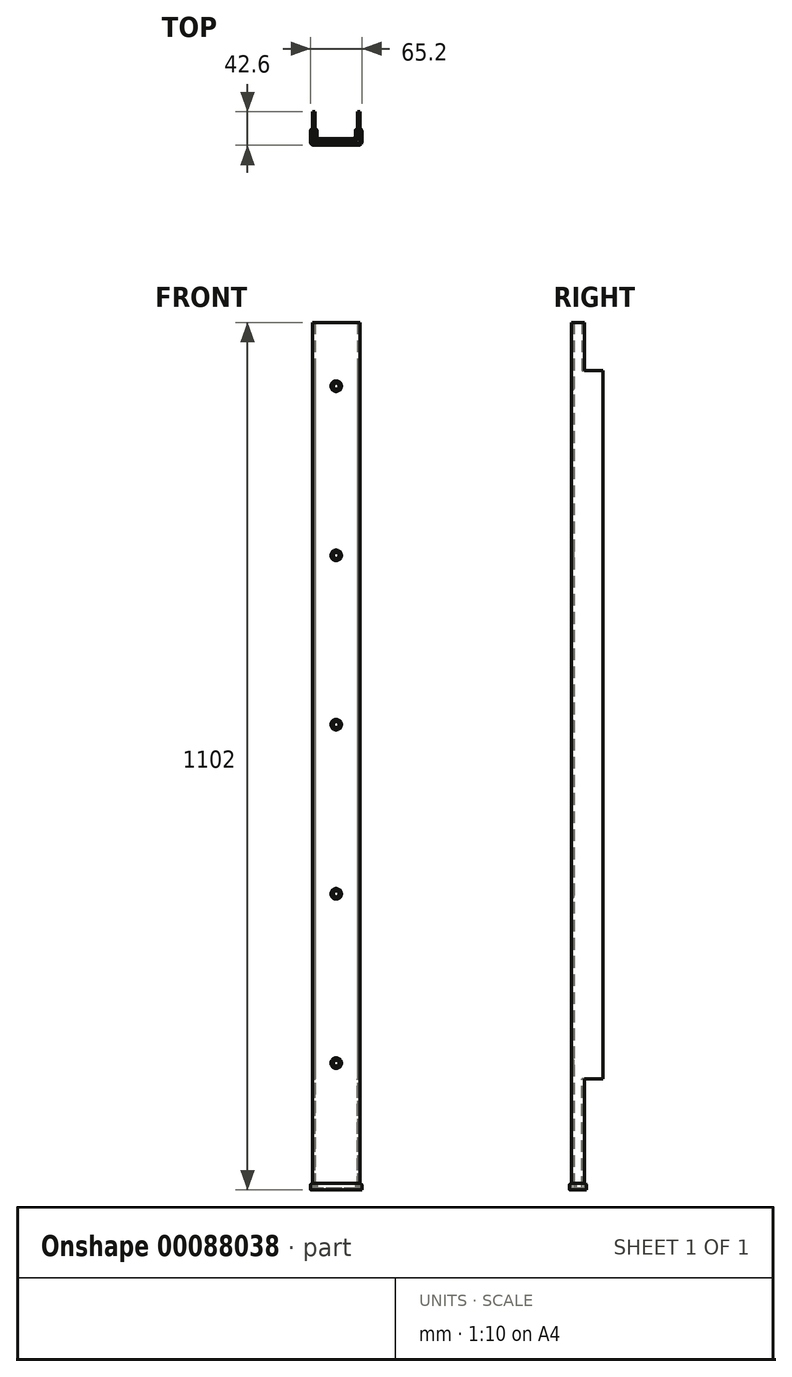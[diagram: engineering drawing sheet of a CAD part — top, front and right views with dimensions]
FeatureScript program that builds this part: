
annotation { "Feature Type Name" : "Feature", "Feature Type Description" : "" }
export const myFeature = defineFeature(function(context is Context, id is Id, definition is map)
    precondition{}
    {
        {
            var Q0;
            Q0=qCreatedBy(makeId("Top.planeOp"),FACE);
            var sketch = newSketch(context, id + "F0", { "sketchPlane" : qUnion([Q0])});
            skLineSegment(sketch, "E0", {"start": v(0, 0) * mm, "end": v(-60, 0) * mm});
            skLineSegment(sketch, "E1", {"start": v(-60, 0) * mm, "end": v(-60, 40) * mm});
            skLineSegment(sketch, "E2", {"start": v(0, 0) * mm, "end": v(0, 40) * mm});
            skLineSegment(sketch, "E3.0", {"start": v(-57, 3) * mm, "end": v(-57, 40) * mm});
            skLineSegment(sketch, "E3.1", {"start": v(-3, 3) * mm, "end": v(-57, 3) * mm});
            skLineSegment(sketch, "E3.2", {"start": v(-3, 3) * mm, "end": v(-3, 40) * mm});
            skLineSegment(sketch, "E4", {"start": v(-60, 40) * mm, "end": v(-57, 40) * mm});
            skLineSegment(sketch, "E5", {"start": v(0, 40) * mm, "end": v(-3, 40) * mm});
            skSolve(sketch);
        }
        {
            var Q0;
            Q0=makeQuery(id+"F0.imprint","IMPRINT",FACE,{"disambiguationData":[TD([[makeQuery(id+"F0.imprint","IMPRINT",EDGE,{"derivedFrom":sQuery(id+"F0.wireOp",EDGE,"E0")}),-1.0]])]});
            extrude(context, id + "F1", {"entities" : qUnion([Q0]), "depth" : 1100 * mm});
        }
        {
            assignVariable(context, id + "F2", {"name" : "extrusion_width", "anyValue" : 0.48});
        }
        {
            assignVariable(context, id + "F3", {"name" : "wall", "anyValue" : 5 * getVariable(context, 'extrusion_width')});
        }
        {
            assignVariable(context, id + "F4", {"name" : "foot_height", "anyValue" : 8});
        }
        {
            assignVariable(context, id + "F5", {"name" : "floor_thickness", "anyValue" : 2});
        }
        {
            var Q0;
            Q0=qCreatedBy(makeId("Top.planeOp"),FACE);
            cPlane(context, id + "F6", {"entities" : qUnion([Q0]), "cplaneType" : CPlaneType.OFFSET, "offset" : 139 * mm, "width" : 150 * mm, "height" : 150 * mm});
        }
        {
            var Q0;
            Q0=qCreatedBy(id+"F6.planeOp",FACE);
            var sketch = newSketch(context, id + "F7", { "sketchPlane" : qUnion([Q0])});
            skCircle(sketch, "E6", {"center": v(-30, 43) * mm, "radius": 40 * mm});
            skLineSegment(sketch, "E7.0", {"start": v(-3, 3) * mm, "end": v(-57, 3) * mm, "construction": true});
            skPoint(sketch, "E8", {"position": v(-30, 3) * mm});
            skSolve(sketch);
        }
        {
            var Q0;
            Q0=makeQuery(id+"F7.imprint","IMPRINT",FACE,{"disambiguationData":[TD([[makeQuery(id+"F7.imprint","IMPRINT",EDGE,{"derivedFrom":sQuery(id+"F7.wireOp",EDGE,"E6")}),1.0]])]});
            var Q1;
            Q1=makeQuery(id+"F1.opExtrude","CAP_FACE",FACE,{"disambiguationData":[OSD([sQuery(id+"F0.wireOp",EDGE,"E0"),sQuery(id+"F0.wireOp",EDGE,"E1"),sQuery(id+"F0.wireOp",EDGE,"E2"),sQuery(id+"F0.wireOp",EDGE,"E3.0"),sQuery(id+"F0.wireOp",EDGE,"E3.1"),sQuery(id+"F0.wireOp",EDGE,"E3.2"),sQuery(id+"F0.wireOp",EDGE,"E4"),sQuery(id+"F0.wireOp",EDGE,"E5")])],"isStart":true});
            extrude(context, id + "F8", {"entities" : qUnion([Q0]), "operationType" : NewBodyOperationType.REMOVE, "endBound" : BoundingType.UP_TO_SURFACE, "oppositeDirection" : true, "endBoundEntityFace" : qUnion([Q1]), "depth" : 66.5 * mm});
        }
        {
            var Q0;
            Q0=qCreatedBy(id+"F6.planeOp",FACE);
            cPlane(context, id + "F9", {"entities" : qUnion([Q0]), "cplaneType" : CPlaneType.OFFSET, "offset" : 900 * mm, "width" : 150 * mm, "height" : 150 * mm});
        }
        {
            var Q0;
            Q0=qCreatedBy(id+"F9.planeOp",FACE);
            var sketch = newSketch(context, id + "F10", { "sketchPlane" : qUnion([Q0])});
            skCircle(sketch, "E9.0", {"center": v(-30, 43) * mm, "radius": 40 * mm});
            skLineSegment(sketch, "E10.0", {"start": v(-3, 3) * mm, "end": v(-57, 3) * mm, "construction": true});
            skLineSegment(sketch, "E11", {"start": v(-30, 43) * mm, "end": v(-30, 3) * mm, "construction": true});
            skLineSegment(sketch, "E12", {"start": v(-30, 43) * mm, "end": v(-64.64, 23) * mm, "construction": true});
            skLineSegment(sketch, "E13.MirrorCS", {"start": v(-30, 43) * mm, "end": v(4.64, 23) * mm, "construction": true});
            skLineSegment(sketch, "E14", {"start": v(-64.64, 23) * mm, "end": v(-113.65, 107.9) * mm, "construction": true});
            skLineSegment(sketch, "E15.MirrorCS", {"start": v(4.64, 23) * mm, "end": v(53.65, 107.9) * mm, "construction": true});
            skCircle(sketch, "E16", {"center": v(-30, 70) * mm, "radius": 6.5 * mm, "construction": true});
            skSolve(sketch);
        }
        {
            var Q0;
            Q0=makeQuery(id+"F10.imprint","IMPRINT",FACE,{"disambiguationData":[TD([[makeQuery(id+"F10.imprint","IMPRINT",EDGE,{"derivedFrom":sQuery(id+"F10.wireOp",EDGE,"E9.0")}),1.0]])]});
            var Q1;
            Q1=makeQuery(id+"F1.opExtrude","CAP_FACE",FACE,{"disambiguationData":[OSD([sQuery(id+"F0.wireOp",EDGE,"E0"),sQuery(id+"F0.wireOp",EDGE,"E1"),sQuery(id+"F0.wireOp",EDGE,"E2"),sQuery(id+"F0.wireOp",EDGE,"E3.0"),sQuery(id+"F0.wireOp",EDGE,"E3.1"),sQuery(id+"F0.wireOp",EDGE,"E3.2"),sQuery(id+"F0.wireOp",EDGE,"E4"),sQuery(id+"F0.wireOp",EDGE,"E5")])],"isStart":false});
            extrude(context, id + "F11", {"entities" : qUnion([Q0]), "operationType" : NewBodyOperationType.REMOVE, "endBound" : BoundingType.UP_TO_SURFACE, "endBoundEntityFace" : qUnion([Q1]), "depth" : 26 * mm});
        }
        {
            var Q0;
            Q0=makeQuery(id+"F1.opExtrude","SWEPT_FACE",FACE,{"disambiguationData":[OSD([sQuery(id+"F0.wireOp",EDGE,"E0")])]});
            var sketch = newSketch(context, id + "F12", { "sketchPlane" : qUnion([Q0])});
            skLineSegment(sketch, "E17", {"start": v(-60, 550) * mm, "end": v(0, 550) * mm, "construction": true});
            skLineSegment(sketch, "E18", {"start": v(0, 139) * mm, "end": v(-60, 139) * mm, "construction": true});
            skLineSegment(sketch, "E19", {"start": v(-60, 1039) * mm, "end": v(0, 1039) * mm, "construction": true});
            skLineSegment(sketch, "E20", {"start": v(-30, 139) * mm, "end": v(-30, 1039) * mm, "construction": true});
            skPoint(sketch, "E21", {"position": v(-30, 159) * mm});
            skPoint(sketch, "E22.1.0.0", {"position": v(-30, 374) * mm});
            skPoint(sketch, "E22.2.0.0", {"position": v(-30, 589) * mm});
            skPoint(sketch, "E22.3.0.0", {"position": v(-30, 804) * mm});
            skPoint(sketch, "E22.4.0.0", {"position": v(-30, 1019) * mm});
            skLineSegment(sketch, "E22.direction1", {"start": v(-30, 159) * mm, "end": v(-30, 374) * mm, "construction": true});
            skLineSegment(sketch, "E23", {"start": v(-30, 139) * mm, "end": v(-30, 159) * mm, "construction": true});
            skLineSegment(sketch, "E24", {"start": v(-30, 1019) * mm, "end": v(-30, 1039) * mm, "construction": true});
            skSolve(sketch);
        }
        {
            var Q0;
            Q0=sQuery(id+"F12.wireOp",VERTEX,"E23.end");
            var Q1;
            Q1=sQuery(id+"F12.wireOp",VERTEX,"E22.1.0.0");
            var Q2;
            Q2=sQuery(id+"F12.wireOp",VERTEX,"E22.2.0.0");
            var Q3;
            Q3=sQuery(id+"F12.wireOp",VERTEX,"E22.3.0.0");
            var Q4;
            Q4=sQuery(id+"F12.wireOp",VERTEX,"E22.4.0.0");
            var Q5;
            Q5=makeQuery(id+"F1.opExtrude","SWEPT_BODY",BODY,{"disambiguationData":[OSD([sQuery(id+"F0.wireOp",EDGE,"E0"),sQuery(id+"F0.wireOp",EDGE,"E1"),sQuery(id+"F0.wireOp",EDGE,"E2"),sQuery(id+"F0.wireOp",EDGE,"E3.0"),sQuery(id+"F0.wireOp",EDGE,"E3.1"),sQuery(id+"F0.wireOp",EDGE,"E3.2"),sQuery(id+"F0.wireOp",EDGE,"E4"),sQuery(id+"F0.wireOp",EDGE,"E5")])]});
            hole(context, id + "F13", {"style" : HoleStyle.C_SINK, "endStyle" : HoleEndStyle.THROUGH, "standardTappedOrClearance" : lookupTablePath({ "standard" : "ISO", "fit" : "Normal", "size" : "M6", "type" : "Clearance" }), "standardBlindInLast" : lookupTablePath({ "fit" : "Standard", "standard" : "ISO", "size" : "M6", "type" : "Clearance" }), "holeDiameter" : 6.6 * mm, "cSinkDiameter" : 13.44 * mm, "cSinkAngle" : 90 * degree, "locations" : qUnion([Q0, Q1, Q2, Q3, Q4]), "scope" : qUnion([Q5]), "isTappedThrough" : true});
        }
        {
            var Q0;
            Q0=makeQuery(id+"F1.opExtrude","CAP_FACE",FACE,{"disambiguationData":[OSD([sQuery(id+"F0.wireOp",EDGE,"E0"),sQuery(id+"F0.wireOp",EDGE,"E1"),sQuery(id+"F0.wireOp",EDGE,"E2"),sQuery(id+"F0.wireOp",EDGE,"E3.0"),sQuery(id+"F0.wireOp",EDGE,"E3.1"),sQuery(id+"F0.wireOp",EDGE,"E3.2"),sQuery(id+"F0.wireOp",EDGE,"E4"),sQuery(id+"F0.wireOp",EDGE,"E5")])],"isStart":true});
            var sketch = newSketch(context, id + "F14", { "sketchPlane" : qUnion([Q0])});
            skLineSegment(sketch, "E25.1", {"start": v(0.2, 0.2) * mm, "end": v(-60.2, 0.2) * mm});
            skLineSegment(sketch, "E26.1", {"start": v(-3.2, -3.2) * mm, "end": v(-56.8, -3.2) * mm});
            skLineSegment(sketch, "E27", {"start": v(0.2, 0.2) * mm, "end": v(0.2, -16.74) * mm});
            skLineSegment(sketch, "E28", {"start": v(0.2, -16.74) * mm, "end": v(-3.2, -16.74) * mm});
            skLineSegment(sketch, "E29", {"start": v(-3.2, -16.74) * mm, "end": v(-3.2, -3.2) * mm});
            skLineSegment(sketch, "E30", {"start": v(-56.8, -3.2) * mm, "end": v(-56.8, -16.74) * mm});
            skLineSegment(sketch, "E31", {"start": v(-56.8, -16.74) * mm, "end": v(-60.2, -16.74) * mm});
            skLineSegment(sketch, "E32", {"start": v(-60.2, -16.74) * mm, "end": v(-60.2, 0.2) * mm});
            skLineSegment(sketch, "E33.0", {"start": v(2.6, 2.6) * mm, "end": v(-62.6, 2.6) * mm});
            skLineSegment(sketch, "E33.1", {"start": v(-62.6, -19.14) * mm, "end": v(-62.6, 2.6) * mm});
            skLineSegment(sketch, "E33.2", {"start": v(2.6, 2.6) * mm, "end": v(2.6, -19.14) * mm});
            skLineSegment(sketch, "E33.3", {"start": v(-54.4, -19.14) * mm, "end": v(-62.6, -19.14) * mm});
            skLineSegment(sketch, "E33.4", {"start": v(2.6, -19.14) * mm, "end": v(-5.6, -19.14) * mm});
            skLineSegment(sketch, "E33.5", {"start": v(-5.6, -19.14) * mm, "end": v(-5.6, -5.6) * mm});
            skLineSegment(sketch, "E33.6", {"start": v(-5.6, -5.6) * mm, "end": v(-54.4, -5.6) * mm});
            skLineSegment(sketch, "E33.7", {"start": v(-54.4, -5.6) * mm, "end": v(-54.4, -19.14) * mm});
            skSolve(sketch);
        }
        {
            var Q0;
            Q0=makeQuery(id+"F14.imprint","IMPRINT",FACE,{"disambiguationData":[TD([[makeQuery(id+"F14.imprint","IMPRINT",EDGE,{"derivedFrom":sQuery(id+"F14.wireOp",EDGE,"E25.1")}),-1.0]])]});
            extrude(context, id + "F15", {"entities" : qUnion([Q0]), "oppositeDirection" : true, "depth" : (getVariable(context, 'foot_height') - getVariable(context, 'floor_thickness')) * mm});
        }
        {
            var Q0;
            Q0=makeQuery(id+"F14.imprint","IMPRINT",FACE,{"disambiguationData":[TD([[makeQuery(id+"F14.imprint","IMPRINT",EDGE,{"derivedFrom":sQuery(id+"F14.wireOp",EDGE,"E25.1")}),1.0]])]});
            var Q1;
            Q1=makeQuery(id+"F14.imprint","IMPRINT",FACE,{"disambiguationData":[TD([[makeQuery(id+"F14.imprint","IMPRINT",EDGE,{"derivedFrom":sQuery(id+"F14.wireOp",EDGE,"E25.1")}),-1.0]])]});
            var Q2;
            {var subQ3=sQuery(id+"F0.wireOp",EDGE,"E0");Q2=makeQuery(id+"F14.imprint","IMPRINT",FACE,{"disambiguationData":[TD([[makeQuery(id+"F14.imprint","IMPRINT",EDGE,{"derivedFrom":makeQuery(id+"F1.opExtrude","CAP_EDGE",EDGE,{"disambiguationData":[OSD([subQ3])],"isStart":true})}),1.0]])]});}
            extrude(context, id + "F16", {"entities" : qUnion([Q0, Q1, Q2]), "operationType" : NewBodyOperationType.ADD, "depth" : (getVariable(context, 'floor_thickness')) * mm});
        }
        {
            var Q0;
            {var subQ0=sQuery(id+"F14.wireOp",EDGE,"E33.4");var subQ1=sQuery(id+"F14.wireOp",EDGE,"E33.2");Q0=makeQuery(id+"F16.boolean.opBoolean","MERGE",EDGE,{"derivedFrom":[makeQuery(id+"F15.opExtrude","SWEPT_EDGE",EDGE,{"disambiguationData":[OSD([subQ1,subQ0])]}),makeQuery(id+"F16.opExtrude","SWEPT_EDGE",EDGE,{"disambiguationData":[OSD([subQ1,subQ0])]})]});}
            var Q1;
            {var subQ0=sQuery(id+"F14.wireOp",EDGE,"E33.5");var subQ1=sQuery(id+"F14.wireOp",EDGE,"E33.4");Q1=makeQuery(id+"F16.boolean.opBoolean","MERGE",EDGE,{"derivedFrom":[makeQuery(id+"F15.opExtrude","SWEPT_EDGE",EDGE,{"disambiguationData":[OSD([subQ1,subQ0])]}),makeQuery(id+"F16.opExtrude","SWEPT_EDGE",EDGE,{"disambiguationData":[OSD([subQ1,subQ0])]})]});}
            var Q2;
            {var subQ0=sQuery(id+"F14.wireOp",EDGE,"E33.6");var subQ1=sQuery(id+"F14.wireOp",EDGE,"E33.5");Q2=makeQuery(id+"F16.boolean.opBoolean","MERGE",EDGE,{"derivedFrom":[makeQuery(id+"F15.opExtrude","SWEPT_EDGE",EDGE,{"disambiguationData":[OSD([subQ1,subQ0])]}),makeQuery(id+"F16.opExtrude","SWEPT_EDGE",EDGE,{"disambiguationData":[OSD([subQ1,subQ0])]})]});}
            var Q3;
            {var subQ0=sQuery(id+"F14.wireOp",EDGE,"E33.7");var subQ1=sQuery(id+"F14.wireOp",EDGE,"E33.3");Q3=makeQuery(id+"F16.boolean.opBoolean","MERGE",EDGE,{"derivedFrom":[makeQuery(id+"F15.opExtrude","SWEPT_EDGE",EDGE,{"disambiguationData":[OSD([subQ1,subQ0])]}),makeQuery(id+"F16.opExtrude","SWEPT_EDGE",EDGE,{"disambiguationData":[OSD([subQ1,subQ0])]})]});}
            var Q4;
            {var subQ0=sQuery(id+"F14.wireOp",EDGE,"E33.3");var subQ1=sQuery(id+"F14.wireOp",EDGE,"E33.1");Q4=makeQuery(id+"F16.boolean.opBoolean","MERGE",EDGE,{"derivedFrom":[makeQuery(id+"F15.opExtrude","SWEPT_EDGE",EDGE,{"disambiguationData":[OSD([subQ1,subQ0])]}),makeQuery(id+"F16.opExtrude","SWEPT_EDGE",EDGE,{"disambiguationData":[OSD([subQ1,subQ0])]})]});}
            var Q5;
            {var subQ0=sQuery(id+"F14.wireOp",EDGE,"E33.7");var subQ1=sQuery(id+"F14.wireOp",EDGE,"E33.6");Q5=makeQuery(id+"F16.boolean.opBoolean","MERGE",EDGE,{"derivedFrom":[makeQuery(id+"F15.opExtrude","SWEPT_EDGE",EDGE,{"disambiguationData":[OSD([subQ1,subQ0])]}),makeQuery(id+"F16.opExtrude","SWEPT_EDGE",EDGE,{"disambiguationData":[OSD([subQ1,subQ0])]})]});}
            var Q6;
            {var subQ0=sQuery(id+"F14.wireOp",EDGE,"E33.1");var subQ1=sQuery(id+"F14.wireOp",EDGE,"E33.0");Q6=makeQuery(id+"F16.boolean.opBoolean","MERGE",EDGE,{"derivedFrom":[makeQuery(id+"F15.opExtrude","SWEPT_EDGE",EDGE,{"disambiguationData":[OSD([subQ1,subQ0])]}),makeQuery(id+"F16.opExtrude","SWEPT_EDGE",EDGE,{"disambiguationData":[OSD([subQ1,subQ0])]})]});}
            var Q7;
            {var subQ0=sQuery(id+"F14.wireOp",EDGE,"E33.2");var subQ1=sQuery(id+"F14.wireOp",EDGE,"E33.0");Q7=makeQuery(id+"F16.boolean.opBoolean","MERGE",EDGE,{"derivedFrom":[makeQuery(id+"F15.opExtrude","SWEPT_EDGE",EDGE,{"disambiguationData":[OSD([subQ1,subQ0])]}),makeQuery(id+"F16.opExtrude","SWEPT_EDGE",EDGE,{"disambiguationData":[OSD([subQ1,subQ0])]})]});}
            fillet(context, id + "F17", {"entities" : qUnion([Q0, Q1, Q2, Q3, Q4, Q5, Q6, Q7]), "radius" : (getVariable(context, 'wall') + 3 / 2) * mm, "tangentPropagation" : true, "allowEdgeOverflow" : false});
        }
        {
            var Q0;
            Q0=makeQuery(id+"F15.opExtrude","CAP_EDGE",EDGE,{"disambiguationData":[OSD([sQuery(id+"F14.wireOp",EDGE,"E33.2")])],"isStart":false});
            var Q1;
            Q1=makeQuery(id+"F15.opExtrude","SWEPT_EDGE",EDGE,{"disambiguationData":[OSD([sQuery(id+"F14.wireOp",EDGE,"E26.1"),sQuery(id+"F14.wireOp",EDGE,"E29")])]});
            var Q2;
            Q2=makeQuery(id+"F15.opExtrude","SWEPT_EDGE",EDGE,{"disambiguationData":[OSD([sQuery(id+"F14.wireOp",EDGE,"E26.1"),sQuery(id+"F14.wireOp",EDGE,"E30")])]});
            fillet(context, id + "F18", {"entities" : qUnion([Q0, Q1, Q2]), "radius" : 2 * mm, "tangentPropagation" : true, "allowEdgeOverflow" : false});
        }
    });
